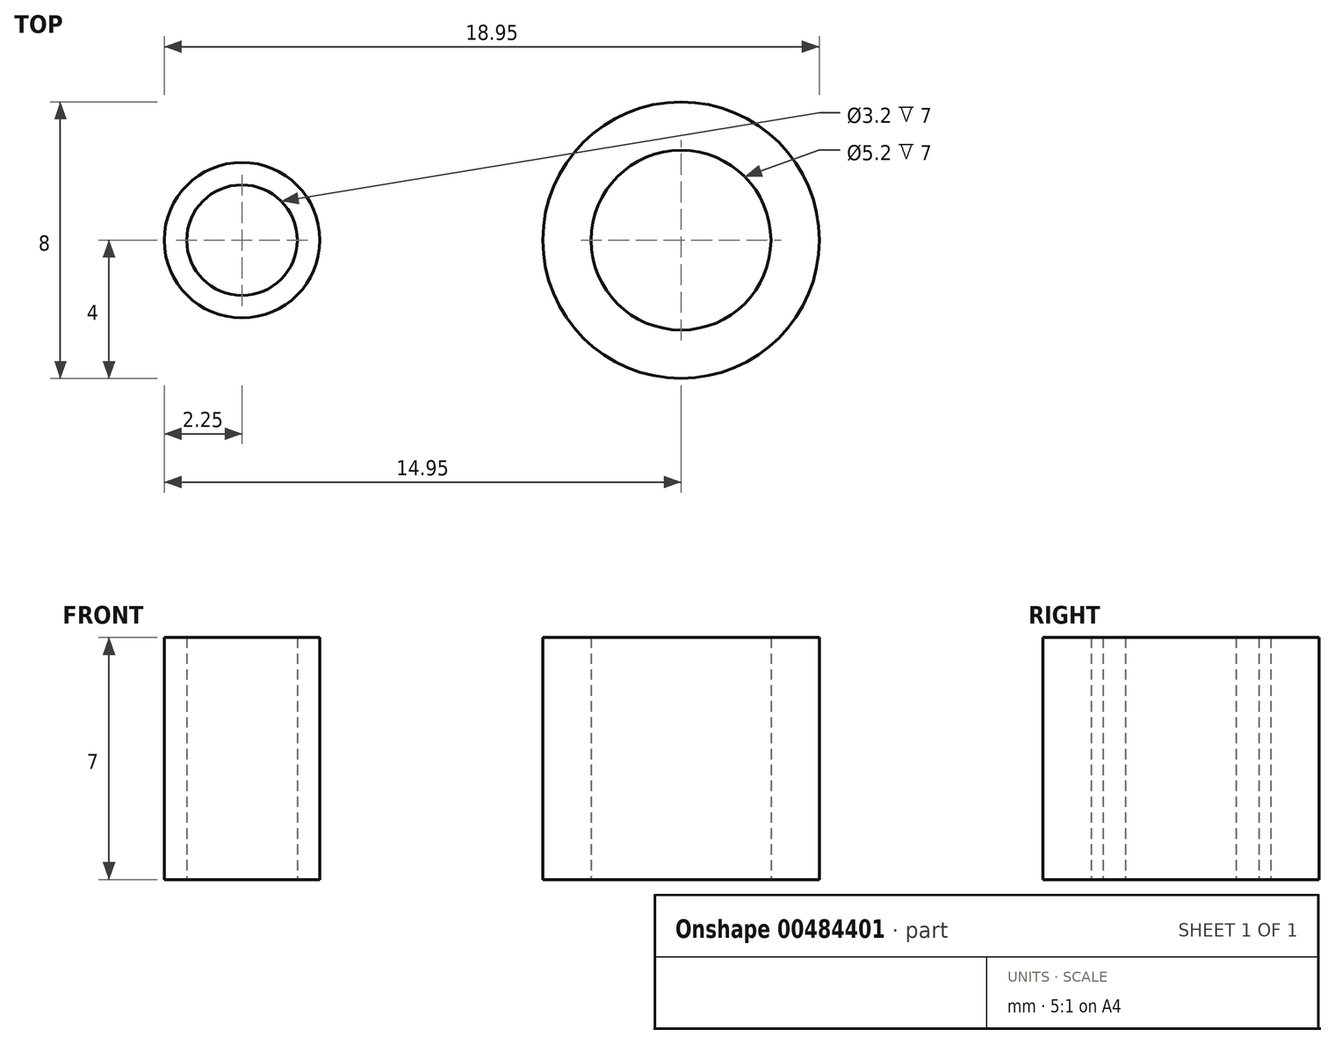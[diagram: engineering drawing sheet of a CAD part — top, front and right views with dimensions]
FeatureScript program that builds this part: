
annotation { "Feature Type Name" : "Feature", "Feature Type Description" : "" }
export const myFeature = defineFeature(function(context is Context, id is Id, definition is map)
    precondition{}
    {
        {
            var Q0;
            Q0=qCreatedBy(makeId("Top.planeOp"), FACE);
            var sketch = newSketch(context, id + "F0", { "sketchPlane" : qUnion([Q0]), "disableImprinting" : false});
            skCircle(sketch, "E0", {"center": v(0, 0) * mm, "radius": 2.25 * mm});
            skCircle(sketch, "E1", {"center": v(0, 0) * mm, "radius": 1.6 * mm});
            skCircle(sketch, "E2", {"center": v(12.7, 0) * mm, "radius": 4 * mm});
            skCircle(sketch, "E3", {"center": v(12.7, 0) * mm, "radius": 2.6 * mm});
            skLineSegment(sketch, "E4", {"start": v(0, 0) * mm, "end": v(12.7, 0) * mm, "construction": true});
            skSolve(sketch);
        }
        {
            var Q0;
            Q0 = qSketchRegion(id + "F0", true);
            extrude(context, id + "F1", {"entities" : qUnion([Q0]), "domain" : OperationDomain.MODEL, "flatOperationType" : FlatOperationType.REMOVE, "depth" : 7 * mm, "offsetDistance" : 25.4 * mm});
        }
    });
